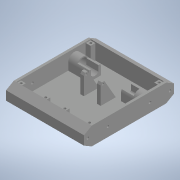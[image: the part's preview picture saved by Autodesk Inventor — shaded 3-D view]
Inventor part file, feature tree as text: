
AUTODESK INVENTOR PART (.ipt)
format: ipt  version: 2020 (Build 240168000, 168)  size: 396,800 bytes
history: native  units: in
note: dims shown in document units (in); Inventor stores cm internally (conversion verified against a paired STEP export)
features: projected_geometry x13, extrude x11, sketch x11, mirror x4, plane x1
ambient origin geometry x8: Origin, YZ Plane, XZ Plane, XY Plane, X Axis, Y Axis, Z Axis, Center Point
bodies: Solid1 (feature_tree)
feature tree (40):
  extrude  "Extrusion1"  Depth=5.9055in
  extrude  "Extrusion2"  TaperAngle=0.0deg  [1 undecoded]
  extrude  "Extrusion3"  Depth=1.063in
  extrude  "Extrusion4"  Depth=0.315in
  extrude  "Extrusion5"  TaperAngle=0.0deg  [1 undecoded]
  extrude  "Extrusion6"  Depth=0.5906in
  mirror  "Mirror1"
  extrude  "Extrusion7"  Depth=0.0787in
  mirror  "Mirror2"
  extrude  "Extrusion8"  Depth=0.5512in
  mirror  "Mirror3"
  plane  "Work Plane1"
  extrude  "Extrusion9"  Depth=0.7874in TaperAngle=0.0deg
  mirror  "Mirror4"
  extrude  "Extrusion10"  Depth=6.063in TaperAngle=0.0deg
  extrude  "Extrusion11"  Depth=0.1575in
  sketch  "Sketch1"  dims[d0=1.1811in d1=5.9055in]
  sketch  "Sketch2"  dims[d2=5.1181in d3=0.0in]
  projected_geometry  "Projected Loop1"
  sketch  "Sketch3"  dims[d4=0.1575in d5=1.063in]
  projected_geometry  "Projected Loop2"
  projected_geometry  "Projected Loop3"
  sketch  "Sketch4"  dims[d6=0.0in d8=0.315in]
  sketch  "Sketch5"  dims[d10=0.993in d11=0.0in]
  projected_geometry  "Projected Loop4"
  sketch  "Sketch6"  dims[d12=0.6496in d13=0.5906in]
  sketch  "Sketch7"  dims[d14=1.5748in d15=0.0787in]
  sketch  "Sketch9"  dims[d16=0.5512in d17=0.0in d18=0.6102in]
  sketch  "Sketch10"  dims[d19=0.4803in d20=0.7874in d21=0.0in]
  sketch  "Sketch12"  dims[d22=0.1654in d23=6.063in d24=0.0in]
  projected_geometry  "Projected Loop6"
  projected_geometry  "Projected Loop7"
  projected_geometry  "Projected Loop8"
  sketch  "Sketch13"  dims[d25=0.5114in d26=0.1575in d27=1.5748in d28=0.0in d29=0.0in d30=0.1575in d31=0.2756in d32=0.0in d33=0.4331in d34=0.122in d38=2.7559in d40=0.061in d41=0.0909in d42=0.2362in d43=0.0in d44=60.0deg d45=0.0787in d46=0.315in d48=0.993in d49=0.0in d51=0.1575in d52=0.1575in d53=0.2756in d54=0.0in d55=0.4724in]
  projected_geometry  "Projected Loop9"
  projected_geometry  "Projected Loop10"
  projected_geometry  "Projected Loop11"
  projected_geometry  "Projected Loop12"
  projected_geometry  "Projected Loop13"
  projected_geometry  "Projected Loop14"
note: 2 required parameter values undecoded (feature->parameter linkage not recoverable at this tier; creation-order binding heuristic only, values carry confidence <= 0.55)
